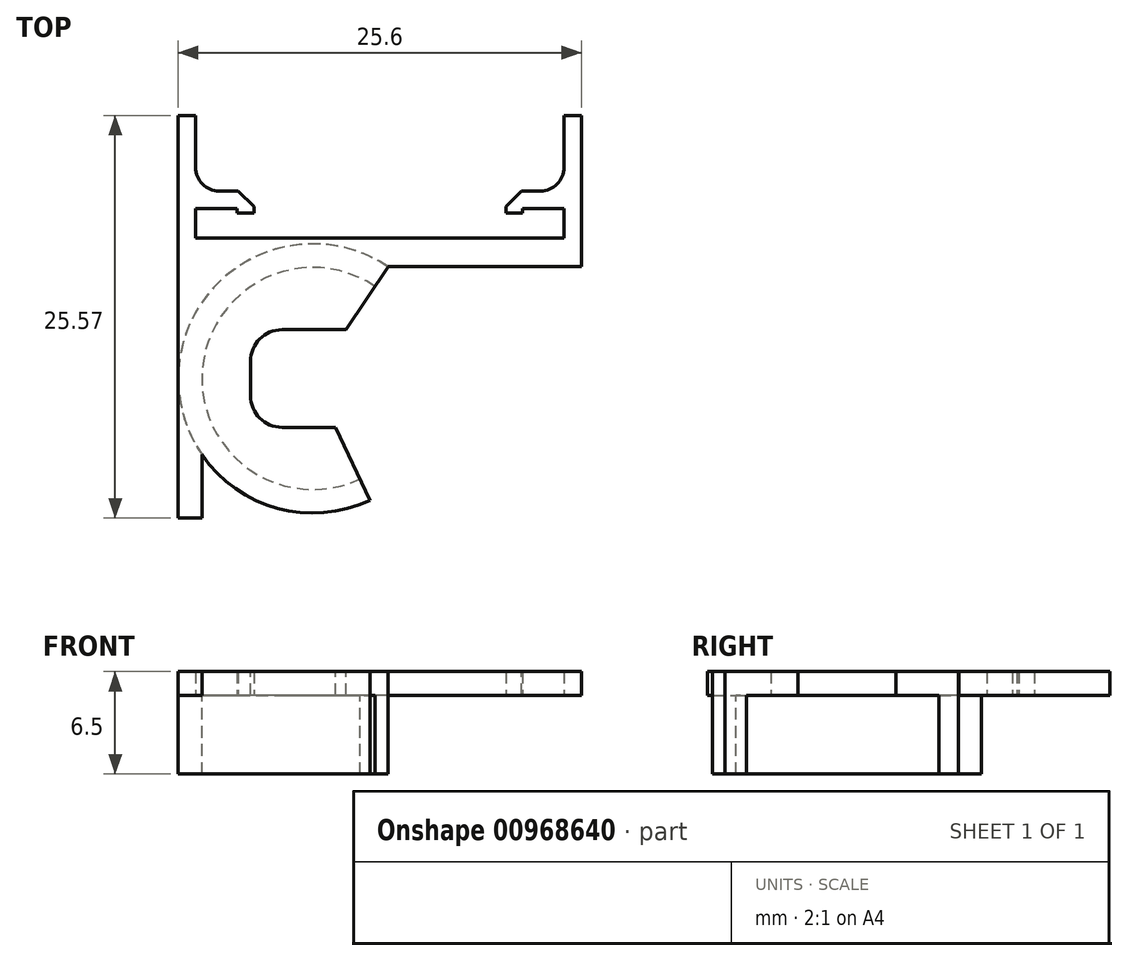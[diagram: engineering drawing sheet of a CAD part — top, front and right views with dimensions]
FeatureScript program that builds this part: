
annotation { "Feature Type Name" : "Feature", "Feature Type Description" : "" }
export const myFeature = defineFeature(function(context is Context, id is Id, definition is map)
    precondition{}
    {
        {
            var Q0;
            Q0=qCreatedBy(makeId("Top.planeOp"),FACE);
            var sketch = newSketch(context, id + "F0", { "sketchPlane" : qUnion([Q0])});
            skCircle(sketch, "E0", {"center": v(0, 0) * mm, "radius": 7.05 * mm});
            skCircle(sketch, "E1", {"center": v(0, 0) * mm, "radius": 8.55 * mm});
            skLineSegment(sketch, "E2", {"start": v(-8.55, 0) * mm, "end": v(-8.55, -8.87) * mm});
            skLineSegment(sketch, "E3", {"start": v(0, 0) * mm, "end": v(6.47, 9.59) * mm});
            skLineSegment(sketch, "E4", {"start": v(0, 0) * mm, "end": v(4.46, -9.57) * mm});
            skLineSegment(sketch, "E5.bottom", {"start": v(15.95, 8.9) * mm, "end": v(-7.45, 8.9) * mm});
            skPoint(sketch, "E5.middle", {"position": v(0, 13.17) * mm});
            skLineSegment(sketch, "E6", {"start": v(-8.55, 10.5) * mm, "end": v(-8.55, 11.9) * mm});
            skLineSegment(sketch, "E7", {"start": v(-8.55, 11.9) * mm, "end": v(-3.75, 11.9) * mm});
            skLineSegment(sketch, "E8", {"start": v(-3.75, 11.9) * mm, "end": v(-3.75, 10.8) * mm});
            skLineSegment(sketch, "E9", {"start": v(-8.55, 0) * mm, "end": v(-8.55, 10.5) * mm});
            skLineSegment(sketch, "E10", {"start": v(15.45, 7.1) * mm, "end": v(4.76, 7.1) * mm});
            skLineSegment(sketch, "E11", {"start": v(15.45, 7.1) * mm, "end": v(17.05, 7.1) * mm});
            skPoint(sketch, "E12.endSnap0", {"position": v(4.25, 8.9) * mm});
            skLineSegment(sketch, "E13", {"start": v(17.05, 7.1) * mm, "end": v(17.05, 11.9) * mm});
            skLineSegment(sketch, "E14", {"start": v(17.05, 11.9) * mm, "end": v(12.25, 11.9) * mm});
            skLineSegment(sketch, "E15", {"start": v(12.25, 11.9) * mm, "end": v(12.25, 10.8) * mm});
            skLineSegment(sketch, "E16", {"start": v(15.95, 10.8) * mm, "end": v(15.95, 8.9) * mm});
            skLineSegment(sketch, "E17", {"start": v(-7.45, 8.9) * mm, "end": v(-7.45, 10.8) * mm});
            skLineSegment(sketch, "E18", {"start": v(-7.45, 16.7) * mm, "end": v(-7.45, 11.9) * mm});
            skLineSegment(sketch, "E19", {"start": v(-8.55, -8.87) * mm, "end": v(-7.05, -8.87) * mm});
            skLineSegment(sketch, "E20", {"start": v(-7.05, -8.87) * mm, "end": v(-7.05, -4.84) * mm});
            skLineSegment(sketch, "E21", {"start": v(-4.82, 10.8) * mm, "end": v(-4.82, 10.51) * mm});
            skLineSegment(sketch, "E22", {"start": v(-3.75, 10.8) * mm, "end": v(-3.75, 10.5) * mm});
            skLineSegment(sketch, "E23", {"start": v(-3.75, 10.5) * mm, "end": v(-4.82, 10.51) * mm});
            skLineSegment(sketch, "E24", {"start": v(-7.45, 10.8) * mm, "end": v(-4.82, 10.8) * mm});
            skLineSegment(sketch, "E25", {"start": v(12.25, 10.8) * mm, "end": v(12.25, 10.5) * mm});
            skLineSegment(sketch, "E26", {"start": v(12.25, 10.5) * mm, "end": v(13.32, 10.5) * mm});
            skLineSegment(sketch, "E27", {"start": v(13.32, 10.5) * mm, "end": v(13.32, 10.8) * mm});
            skLineSegment(sketch, "E28", {"start": v(13.32, 10.8) * mm, "end": v(15.95, 10.8) * mm});
            skLineSegment(sketch, "E29", {"start": v(17.05, 11.9) * mm, "end": v(17.05, 16.7) * mm});
            skLineSegment(sketch, "E30", {"start": v(-8.55, 11.9) * mm, "end": v(-8.55, 16.7) * mm});
            skLineSegment(sketch, "E31", {"start": v(-8.55, 16.7) * mm, "end": v(-7.45, 16.7) * mm});
            skLineSegment(sketch, "E32", {"start": v(17.05, 16.7) * mm, "end": v(15.95, 16.7) * mm});
            skLineSegment(sketch, "E33", {"start": v(15.95, 16.7) * mm, "end": v(15.95, 11.9) * mm});
            skSolve(sketch);
        }
        {
            var Q0;
            Q0=makeQuery(id+"F0.imprint","IMPRINT",FACE,{"disambiguationData":[TD([[makeQuery(id+"F0.imprint","IMPRINT",EDGE,{"derivedFrom":sQuery(id+"F0.wireOp",EDGE,"E6")}),-1.0]])]});
            var Q1;
            {var subQ0=sQuery(id+"F0.wireOp",EDGE,"E2");Q1=makeQuery(id+"F0.imprint","IMPRINT",FACE,{"disambiguationData":[TD([[makeQuery(id+"F0.imprint","IMPRINT",EDGE,{"derivedFrom":subQ0}),1.0]])]});}
            var Q2;
            {var subQ4=sQuery(id+"F0.wireOp",EDGE,"E3");var subQ10=sQuery(id+"F0.wireOp",EDGE,"E0");var subQ12=makeQuery(id+"F0.imprint","INTERSECT",VERTEX,{"derivedFrom":[subQ10,subQ4]});Q2=makeQuery(id+"F0.imprint","IMPRINT",FACE,{"disambiguationData":[TD([[makeQuery(id+"F0.imprint","IMPRINT",EDGE,{"disambiguationData":[TD([[subQ12,-1.0]])],"derivedFrom":subQ10}),-1.0]])]});}
            var Q3;
            {var subQ0=sQuery(id+"F0.wireOp",EDGE,"E11");Q3=makeQuery(id+"F0.imprint","IMPRINT",FACE,{"disambiguationData":[TD([[makeQuery(id+"F0.imprint","IMPRINT",EDGE,{"derivedFrom":subQ0}),1.0]])]});}
            var Q4;
            {var subQ0=sQuery(id+"F0.wireOp",EDGE,"E10");var subQ1=sQuery(id+"F0.wireOp",EDGE,"E1");var subQ2=makeQuery(id+"F0.imprint","INTERSECT",VERTEX,{"derivedFrom":[subQ1,subQ0]});Q4=makeQuery(id+"F0.imprint","IMPRINT",FACE,{"disambiguationData":[TD([[makeQuery(id+"F0.imprint","IMPRINT",EDGE,{"disambiguationData":[TD([[subQ2,-1.0]])],"derivedFrom":subQ1}),-1.0]])]});}
            var Q5;
            {var subQ4=sQuery(id+"F0.wireOp",EDGE,"jDVoJdCh-EpXq-Jpd6-BWvk-Mq0RIJepdhxw");Q5=makeQuery(id+"F0.imprint","IMPRINT",FACE,{"disambiguationData":[TD([[makeQuery(id+"F0.imprint","IMPRINT",EDGE,{"derivedFrom":subQ4}),-1.0]])]});}
            var Q6;
            {var subQ2=sQuery(id+"F0.wireOp",EDGE,"E18");Q6=makeQuery(id+"F0.imprint","IMPRINT",FACE,{"disambiguationData":[TD([[makeQuery(id+"F0.imprint","IMPRINT",EDGE,{"derivedFrom":subQ2}),-1.0]])]});}
            var Q7;
            {var subQ0=sQuery(id+"F0.wireOp",EDGE,"E29");Q7=makeQuery(id+"F0.imprint","IMPRINT",FACE,{"disambiguationData":[TD([[makeQuery(id+"F0.imprint","IMPRINT",EDGE,{"derivedFrom":subQ0}),1.0]])]});}
            extrude(context, id + "F1", {"entities" : qUnion([Q0, Q1, Q2, Q3, Q4, Q5, Q6, Q7]), "depth" : 1.5 * mm, "offsetDistance" : 25 * mm});
        }
        {
            var Q0;
            Q0=makeQuery(id+"F1.opExtrude","SWEPT_EDGE",EDGE,{"disambiguationData":[OSD([sQuery(id+"F0.wireOp",EDGE,"E7"),sQuery(id+"F0.wireOp",EDGE,"E8")])]});
            var Q1;
            Q1=makeQuery(id+"F1.opExtrude","SWEPT_EDGE",EDGE,{"disambiguationData":[OSD([sQuery(id+"F0.wireOp",EDGE,"E14"),sQuery(id+"F0.wireOp",EDGE,"E15")])]});
            chamfer(context, id + "F2", {"entities" : qUnion([Q0, Q1]), "width" : 1 * mm, "tangentPropagation" : true});
        }
        {
            var Q0;
            Q0=makeQuery(id+"F1.opExtrude","SWEPT_EDGE",EDGE,{"disambiguationData":[OSD([sQuery(id+"F0.wireOp",EDGE,"E7"),sQuery(id+"F0.wireOp",EDGE,"E18")])]});
            var Q1;
            Q1=makeQuery(id+"F1.opExtrude","SWEPT_EDGE",EDGE,{"disambiguationData":[OSD([sQuery(id+"F0.wireOp",EDGE,"E14"),sQuery(id+"F0.wireOp",EDGE,"E33")])]});
            fillet(context, id + "F3", {"entities" : qUnion([Q0, Q1]), "radius" : 1.5 * mm, "tangentPropagation" : true, "allowEdgeOverflow" : false});
        }
        {
            var Q0;
            Q0=makeQuery(id+"F1.opExtrude","CAP_FACE",FACE,{"disambiguationData":[OSD([sQuery(id+"F0.wireOp",EDGE,"E0"),sQuery(id+"F0.wireOp",EDGE,"E1"),sQuery(id+"F0.wireOp",EDGE,"E2"),sQuery(id+"F0.wireOp",EDGE,"E3"),sQuery(id+"F0.wireOp",EDGE,"E4"),sQuery(id+"F0.wireOp",EDGE,"E5.bottom"),sQuery(id+"F0.wireOp",EDGE,"E6"),sQuery(id+"F0.wireOp",EDGE,"E7"),sQuery(id+"F0.wireOp",EDGE,"E8"),sQuery(id+"F0.wireOp",EDGE,"E9"),sQuery(id+"F0.wireOp",EDGE,"E10"),sQuery(id+"F0.wireOp",EDGE,"E11"),sQuery(id+"F0.wireOp",EDGE,"E13"),sQuery(id+"F0.wireOp",EDGE,"E14"),sQuery(id+"F0.wireOp",EDGE,"E15"),sQuery(id+"F0.wireOp",EDGE,"E16"),sQuery(id+"F0.wireOp",EDGE,"E17"),sQuery(id+"F0.wireOp",EDGE,"E18"),sQuery(id+"F0.wireOp",EDGE,"E19"),sQuery(id+"F0.wireOp",EDGE,"E20"),sQuery(id+"F0.wireOp",EDGE,"E21"),sQuery(id+"F0.wireOp",EDGE,"E22"),sQuery(id+"F0.wireOp",EDGE,"E23"),sQuery(id+"F0.wireOp",EDGE,"E24"),sQuery(id+"F0.wireOp",EDGE,"E25"),sQuery(id+"F0.wireOp",EDGE,"E26"),sQuery(id+"F0.wireOp",EDGE,"E27"),sQuery(id+"F0.wireOp",EDGE,"E28"),sQuery(id+"F0.wireOp",EDGE,"E29"),sQuery(id+"F0.wireOp",EDGE,"E30"),sQuery(id+"F0.wireOp",EDGE,"E31"),sQuery(id+"F0.wireOp",EDGE,"E32"),sQuery(id+"F0.wireOp",EDGE,"E33")])],"isStart":false});
            var sketch = newSketch(context, id + "F4", { "sketchPlane" : qUnion([Q0])});
            skArc(sketch, "E34.0", {"start": v(3.94, 5.84) * mm, "mid": v(-7.03, 0.55) * mm, "end": v(2.98, -6.39) * mm});
            skLineSegment(sketch, "E35.0", {"start": v(2.98, -6.39) * mm, "end": v(3.61, -7.75) * mm});
            skLineSegment(sketch, "E36.bottom", {"start": v(-3.96, -3.1) * mm, "end": v(5.96, -3.1) * mm});
            skLineSegment(sketch, "E36.top", {"start": v(-3.96, 3.1) * mm, "end": v(5.96, 3.1) * mm});
            skLineSegment(sketch, "E36.left", {"start": v(-3.96, -3.1) * mm, "end": v(-3.96, 3.1) * mm});
            skLineSegment(sketch, "E37", {"start": v(3.94, 5.84) * mm, "end": v(2.1, 3.1) * mm});
            skLineSegment(sketch, "E38", {"start": v(2.98, -6.39) * mm, "end": v(1.45, -3.1) * mm});
            skSolve(sketch);
        }
        {
            var Q0;
            Q0=makeQuery(id+"F4.imprint","IMPRINT",FACE,{"disambiguationData":[TD([[makeQuery(id+"F4.imprint","IMPRINT",EDGE,{"derivedFrom":sQuery(id+"F4.wireOp",EDGE,"jCzHCR8s-bfWx-o2qP-mTLF-yVVlBHsdreuo")}),1.0]])]});
            var Q1;
            Q1=makeQuery(id+"F4.imprint","IMPRINT",FACE,{"disambiguationData":[TD([[makeQuery(id+"F4.imprint","IMPRINT",EDGE,{"derivedFrom":sQuery(id+"F4.wireOp",EDGE,"E34.0")}),1.0]])]});
            extrude(context, id + "F5", {"entities" : qUnion([Q0, Q1]), "operationType" : NewBodyOperationType.ADD, "oppositeDirection" : true, "depth" : 1.5 * mm, "offsetDistance" : 25 * mm});
        }
        {
            var Q0;
            {var subQ4=sQuery(id+"F0.wireOp",EDGE,"E3");var subQ8=sQuery(id+"F0.wireOp",EDGE,"E0");var subQ10=makeQuery(id+"F0.imprint","INTERSECT",VERTEX,{"derivedFrom":[subQ8,subQ4]});Q0=makeQuery(id+"F0.imprint","IMPRINT",FACE,{"disambiguationData":[TD([[makeQuery(id+"F0.imprint","IMPRINT",EDGE,{"disambiguationData":[TD([[subQ10,-1.0]])],"derivedFrom":subQ8}),-1.0]])]});}
            extrude(context, id + "F6", {"entities" : qUnion([Q0]), "operationType" : NewBodyOperationType.ADD, "oppositeDirection" : true, "depth" : 5 * mm, "offsetDistance" : 25 * mm});
        }
        {
            var Q0;
            Q0=makeQuery(id+"F5.opExtrude","SWEPT_EDGE",EDGE,{"disambiguationData":[OSD([sQuery(id+"F4.wireOp",EDGE,"E36.top"),sQuery(id+"F4.wireOp",EDGE,"E36.left")])]});
            var Q1;
            Q1=makeQuery(id+"F5.opExtrude","SWEPT_EDGE",EDGE,{"disambiguationData":[OSD([sQuery(id+"F4.wireOp",EDGE,"E36.bottom"),sQuery(id+"F4.wireOp",EDGE,"E36.left")])]});
            fillet(context, id + "F7", {"entities" : qUnion([Q0, Q1]), "radius" : 2 * mm, "tangentPropagation" : true, "allowEdgeOverflow" : false});
        }
    });
